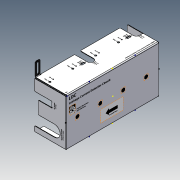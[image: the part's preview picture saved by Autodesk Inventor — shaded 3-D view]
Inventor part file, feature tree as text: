
AUTODESK INVENTOR PART (.ipt)
format: ipt  version: 2020.5 (Build 245400000, 400)  size: 859,136 bytes
history: native  units: mm
features: sketch x17, other x17, sheet_metal_op x7, projected_geometry x6, pattern_linear x1, hole x1, extrude x1, chamfer x1
ambient origin geometry x8: Origin, YZ Plane, XZ Plane, XY Plane, X Axis, Y Axis, Z Axis, Center Point
bodies: Solid1 (feature_tree)
feature tree (51):
  sheet_metal_op  "Face1"
  sheet_metal_op  "Flange1"
  pattern_linear  "Rectangular Pattern1"  Count1=6  [1 undecoded]
  hole  "Hole1"  [1 undecoded]
  extrude  "Extrusion1"  Depth=60.0mm
  sheet_metal_op  "Flange3"
  chamfer  "Corner Round3"
  sketch  "Sketch17"  dims[d17=28.293mm d19=18.0mm]
  sketch  "Sketch18"  dims[d20=60.0mm d21=78.293mm]
  sketch  "Sketch19"  dims[d22=18.0mm]
  sketch  "Sketch20"  dims[d23=60.0mm]
  sketch  "Sketch21"  dims[d24=128.393mm d25=18.0mm d26=60.0mm d27=178.393mm d28=1.0mm d29=0.0mm d38=13.5mm d40=8.373mm d41=1.0mm d42=0.0mm d51=2.0mm d53=2.0mm d55=35.293mm d56=44.043mm d61=94.043mm d62=85.293mm d64=4.0mm d65=4.0mm d66=60.0mm d68=8.0mm d69=4.0mm d70=23.293mm d72=20.0mm d74=100.1mm d75=60.0mm d76=12.92mm d78=30.833mm d79=1.0mm d80=0.0mm d82=23.232mm d88=1.0mm d89=0.0mm d91=70.0mm d92=25.0mm d93=12.5mm d94=29.0mm d95=38.65mm d96=40.306mm d97=43.025mm d98=41.55mm d99=43.025mm d100=41.55mm d101=29.0mm d102=23.251086mm d108=50.0mm d109=23.0mm d110=50.0mm d111=100.1mm d112=150.1mm d113=27.0mm d114=3.5mm d115=6.0mm d116=4.0mm d117=2.0mm d118=90.0deg d119=1.0mm d120=20.594885mm d123=1.0mm d124=1.0mm d125=200.1mm d126=200.685786mm d130=10.0mm d131=27.560906mm d132=30.0mm d133=1.0mm d134=0.0mm d135=10.0mm d136=1.0mm d137=1.0mm d138=0.0mm d149=1.0mm d150=0.5mm d151=2.0mm d152=1.0mm d153=30.0mm d154=90.0deg d155=1.0mm d156=4.0mm d157=1.0mm d158=1.0mm d160=5.0mm d161=18.0mm d162=1.0mm d163=0.0mm d164=35.5mm d165=8.373mm d166=1.0mm d167=0.0mm d168=2.0mm d169=16.6mm d170=6.5mm d171=5.4mm d172=91.2mm d173=2.7mm d174=2.7mm d175=25.6mm d176=4.0mm d177=4.0mm d178=4.3mm d179=14.0mm d186=20.0mm d191=2.2mm d192=18.0mm d217=17.0mm d228=22.9mm d233=4.7mm d234=2.500231mm d239=2.500231mm d244=11.214mm d245=14.914mm d252=10.0mm d264=10.0mm d265=10.0mm d266=10.0mm d330=18.0mm d337=45.0mm d338=45.0mm d343=68.0mm d344=45.0mm d350=45.0mm d369=118.1mm d370=168.1mm d377=50.0mm d385=61.855mm d392=73.05mm d412=19.503mm d419=19.288mm d420=2.6mm d421=9.1mm d422=2.099988mm d423=6.7mm d424=45.55mm d425=45.050107mm d426=36.050101mm d427=46.020973mm d428=2.6mm d429=9.1mm d430=2.099988mm d431=6.7mm d432=45.55mm d433=4.949893mm d434=13.949899mm d435=46.020973mm d436=8.5mm d437=2.1mm d438=2.1mm d439=7.9mm d440=44.306mm d441=23.049893mm d442=22.749893mm d443=47.406mm d444=2.1mm d445=2.0mm d446=2.0mm d447=2.1mm d448=19.999893mm d449=40.256mm d450=40.256mm d451=31.999893mm d452=6.0mm d453=6.5mm d454=2.1mm d455=2.1mm d456=26.7mm d457=38.919893mm d458=38.669893mm d459=29.8mm d460=4.3mm d461=2.1mm d462=6.0mm d463=47.292893mm d464=2.7mm d465=63.873077mm d466=6.0mm d468=2.6mm d469=9.1mm d470=2.099988mm d471=6.7mm d472=45.55mm d473=45.050107mm d474=36.050101mm d475=46.020973mm d476=2.6mm d477=9.2mm d478=2.099988mm d479=6.7mm d480=45.55mm d481=4.949893mm d482=13.949899mm d483=46.020973mm d484=8.5mm d485=2.1mm d486=2.1mm d487=7.9mm d488=44.306mm d489=23.049893mm d490=22.749893mm d491=47.406mm d492=2.1mm d493=2.0mm d494=2.0mm d495=2.1mm d496=19.999893mm d497=40.256mm d498=40.256mm d499=31.999893mm d500=6.0mm d501=6.5mm d502=2.1mm d503=2.1mm d504=26.7mm d505=38.919893mm d506=38.669893mm d507=29.8mm d516=11.8mm d517=2.1mm d518=7.08mm d519=1.33mm d520=3.18mm d521=1.05mm d522=1.05mm d523=3.3mm d524=11.8mm d525=2.1mm d526=7.08mm d527=1.33mm d528=3.18mm d529=1.05mm d530=1.05mm d531=3.3mm d532=17.6mm d533=27.899893mm d534=25.82mm d535=21.92mm d536=25.7mm d537=27.604893mm d538=22.664893mm d539=17.444893mm d540=22.100107mm d541=17.6mm d542=22.395107mm d543=25.82mm d544=21.92mm d545=27.335107mm d546=25.7mm d547=32.555107mm d548=11.8mm d549=2.1mm d550=7.08mm d551=1.33mm d552=3.18mm d553=1.05mm d554=1.05mm d555=3.3mm d556=11.9mm d557=2.1mm d558=7.08mm d559=1.33mm d560=3.18mm d561=1.05mm d562=1.05mm d563=3.3mm d564=17.6mm d565=27.899893mm d566=25.82mm d567=21.92mm d568=25.7mm d569=27.604893mm d570=22.664893mm d571=17.444893mm d572=22.100107mm d573=17.6mm d574=22.395107mm d575=25.82mm d576=21.92mm d577=27.335107mm d578=25.7mm d579=32.555107mm d580=18.6mm d581=2.7mm d582=2.7mm d583=21.1mm d584=17.761013mm d585=4.351086mm d586=16.511013mm d587=8.051086mm d588=2.1mm d589=2.1mm d590=8.9mm d591=13.1mm d592=2.6mm d593=3.3mm d594=1.8mm d595=0.6mm d596=23.909893mm d597=26.009893mm d598=20.194718mm d599=23.294718mm d600=26.905472mm d601=27.908194mm d602=16.158484mm d603=26.020802mm d604=2.7mm d605=19.1mm d606=2.7mm d607=18.6mm d608=36.361013mm d609=4.351086mm d610=36.611013mm d611=8.051086mm d612=2.1mm d613=8.9mm d614=2.1mm d615=15.2mm d616=0.599999mm d617=1.799998mm d618=2.599986mm d619=3.299982mm d620=26.905472mm d621=12.841302mm d622=23.305472mm d623=11.859893mm d624=20.205472mm d625=15.009893mm d626=27.89455mm d627=24.218985mm d629=147.392893mm d639=2.1mm d640=5.4mm d642=39.219893mm d643=23.6mm d644=2.1mm d645=5.5mm d647=39.219893mm d648=23.6mm]
  sketch  "Sketch2"  dims[d0=202.1mm]
  other  "Plate1"
  sketch  "Sketch3"  dims[d1=102.0mm]
  other  "Plate2"
  sheet_metal_op  "Bend1"
  sheet_metal_op  "Corner1"
  sketch  "Sketch4"  dims[d2=1.0mm]
  projected_geometry  "Projected Loop1"
  sketch  "Sketch6"  dims[d3=1.0mm]
  projected_geometry  "Projected Loop3"
  sketch  "Sketch7"  dims[d4=0.5mm]
  projected_geometry  "Projected Loop4"
  sketch  "Sketch8"  dims[d5=2.0mm]
  projected_geometry  "Projected Loop5"
  sketch  "Sketch9"  dims[d6=1.0mm]
  sketch  "Sketch11"  dims[d7=69.4mm d8=90.0deg d9=1.0mm]
  sketch  "Sketch12"  dims[d10=4.0mm]
  projected_geometry  "Projected Loop6"
  sketch  "Sketch14"  dims[d11=1.0mm]
  other  "Plate4"
  sheet_metal_op  "Bend3"
  sheet_metal_op  "Corner3"
  sketch  "Sketch15"  dims[d12=1.0mm]
  projected_geometry  "Projected Loop7"
  sketch  "Sketch16"  dims[d13=18.0mm d14=60.0mm]
  other  "Image1"
  other  "Image2"
  other  "Image3"
  other  "Image4"
  other  "Image5"
  other  "Image6"
  other  "Cut1"
  other  "Cut2"
  other  "Cut3"
  other  "Cut4"
  other  "Cut5"
  other  "Cut6"
  other  "Cut7"
  other  "Definition1"
note: 2 required parameter values undecoded (feature->parameter linkage not recoverable at this tier; creation-order binding heuristic only, values carry confidence <= 0.55)
